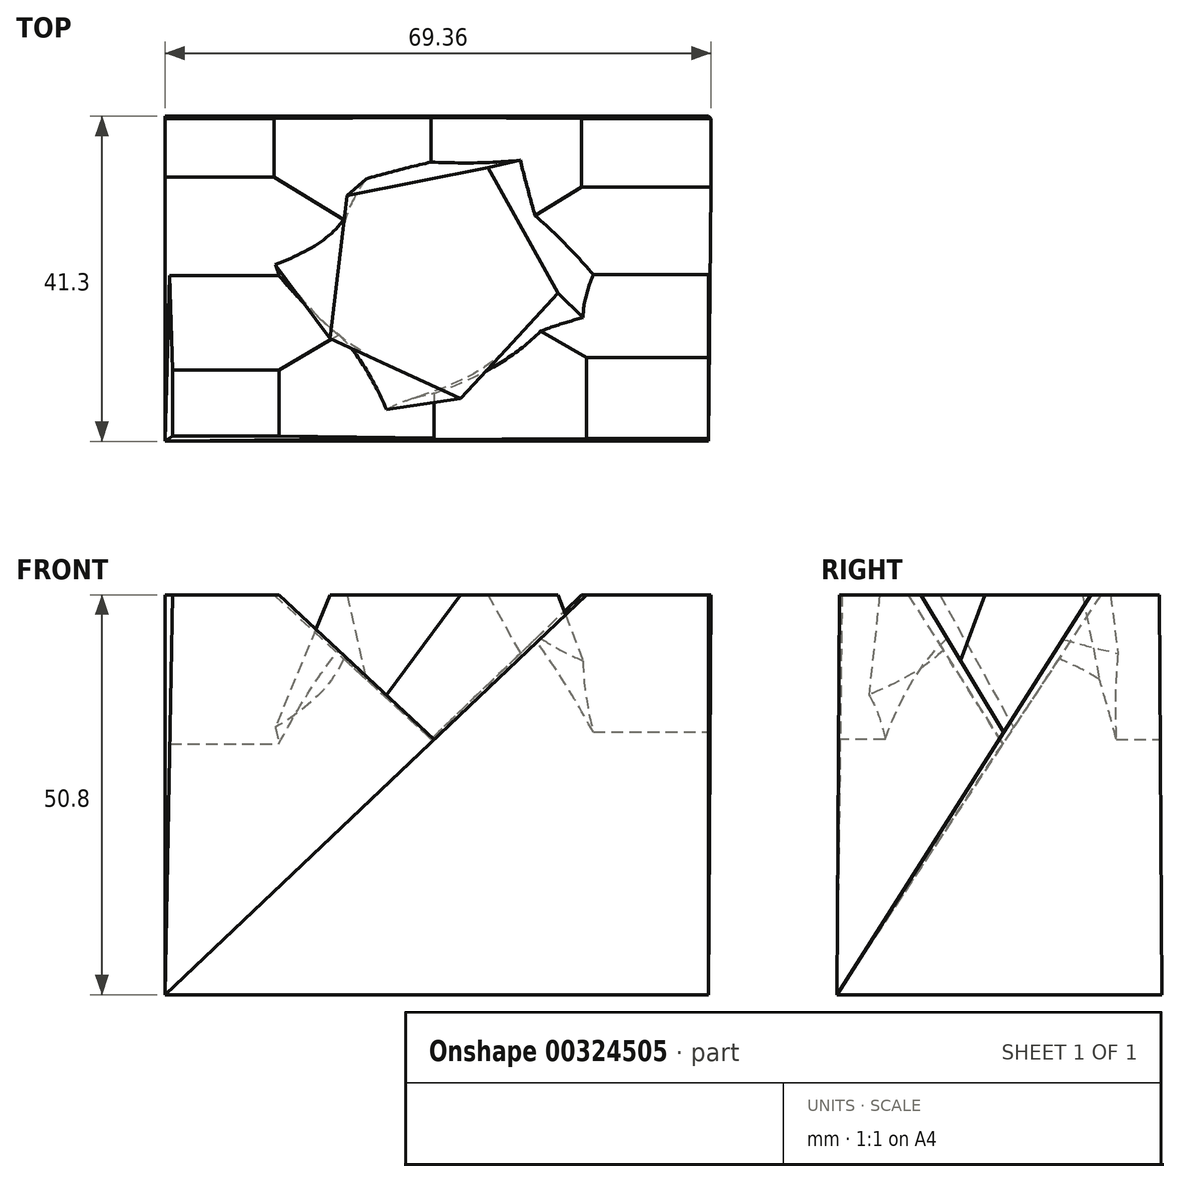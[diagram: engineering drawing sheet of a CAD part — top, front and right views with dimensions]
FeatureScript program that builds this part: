
annotation { "Feature Type Name" : "Feature", "Feature Type Description" : "" }
export const myFeature = defineFeature(function(context is Context, id is Id, definition is map)
    precondition{}
    {
        {
            var Q0;
            Q0=qCreatedBy(makeId("Top.planeOp"),FACE);
            var sketch = newSketch(context, id + "F0", { "sketchPlane" : qUnion([Q0])});
            skLineSegment(sketch, "E0.bottom", {"start": v(34.52, 20.65) * mm, "end": v(-34.52, 20.65) * mm});
            skLineSegment(sketch, "E0.top", {"start": v(34.52, -20.65) * mm, "end": v(-34.52, -20.65) * mm});
            skLineSegment(sketch, "E0.left", {"start": v(34.52, 20.65) * mm, "end": v(34.52, -20.65) * mm});
            skLineSegment(sketch, "E0.right", {"start": v(-34.52, 20.65) * mm, "end": v(-34.52, -20.65) * mm});
            skPoint(sketch, "E0.middle", {"position": v(0, 0) * mm});
            skSolve(sketch);
        }
        {
            var Q0;
            Q0=qCreatedBy(makeId("Top.planeOp"),FACE);
            cPlane(context, id + "F1", {"entities" : qUnion([Q0]), "cplaneType" : CPlaneType.OFFSET, "offset" : 50.8 * mm, "width" : 152.4 * mm, "height" : 152.4 * mm});
        }
        {
            var Q0;
            Q0=qCreatedBy(id+"F1.planeOp",FACE);
            var sketch = newSketch(context, id + "F2", { "sketchPlane" : qUnion([Q0])});
            skLineSegment(sketch, "E1.bottom", {"start": v(-34.52, 20.33) * mm, "end": v(-20.65, 20.33) * mm});
            skLineSegment(sketch, "E1.top", {"start": v(-34.52, 12.9) * mm, "end": v(-20.65, 12.9) * mm});
            skLineSegment(sketch, "E1.left", {"start": v(-34.52, 20.33) * mm, "end": v(-34.52, 12.9) * mm});
            skLineSegment(sketch, "E1.right", {"start": v(-20.65, 20.33) * mm, "end": v(-20.65, 12.9) * mm});
            skLineSegment(sketch, "E2.bottom", {"start": v(34.84, 20.33) * mm, "end": v(18.39, 20.33) * mm});
            skLineSegment(sketch, "E2.top", {"start": v(34.84, 11.61) * mm, "end": v(18.39, 11.61) * mm});
            skLineSegment(sketch, "E2.left", {"start": v(34.84, 20.33) * mm, "end": v(34.84, 11.61) * mm});
            skLineSegment(sketch, "E2.right", {"start": v(18.39, 20.33) * mm, "end": v(18.39, 11.61) * mm});
            skLineSegment(sketch, "E3.bottom", {"start": v(-33.55, -20) * mm, "end": v(-20, -20) * mm});
            skLineSegment(sketch, "E3.top", {"start": v(-33.55, -11.61) * mm, "end": v(-20, -11.61) * mm});
            skLineSegment(sketch, "E3.left", {"start": v(-33.55, -20) * mm, "end": v(-33.55, -11.61) * mm});
            skLineSegment(sketch, "E3.right", {"start": v(-20, -20) * mm, "end": v(-20, -11.61) * mm});
            skLineSegment(sketch, "E4.bottom", {"start": v(34.52, -20.33) * mm, "end": v(19.03, -20.33) * mm});
            skLineSegment(sketch, "E4.top", {"start": v(34.52, -10) * mm, "end": v(19.03, -10) * mm});
            skLineSegment(sketch, "E4.left", {"start": v(34.52, -20.33) * mm, "end": v(34.52, -10) * mm});
            skLineSegment(sketch, "E4.right", {"start": v(19.03, -20.33) * mm, "end": v(19.03, -10) * mm});
            skCircle(sketch, "E5.cCircle", {"center": v(0, 0) * mm, "radius": 12.57 * mm, "construction": true});
            skLineSegment(sketch, "E5.0", {"start": v(6.52, 14.1) * mm, "end": v(15.42, -1.84) * mm});
            skLineSegment(sketch, "E5.1", {"start": v(15.42, -1.84) * mm, "end": v(3.02, -15.24) * mm});
            skLineSegment(sketch, "E5.2", {"start": v(3.02, -15.24) * mm, "end": v(-13.56, -7.58) * mm});
            skLineSegment(sketch, "E5.3", {"start": v(-13.56, -7.58) * mm, "end": v(-11.4, 10.55) * mm});
            skLineSegment(sketch, "E5.4", {"start": v(-11.4, 10.55) * mm, "end": v(6.52, 14.1) * mm});
            skPoint(sketch, "E5.0.midPoint", {"position": v(10.97, 6.13) * mm});
            skSolve(sketch);
        }
        {
            var Q0;
            Q0=makeQuery(id+"F0.imprint","IMPRINT",FACE,{"disambiguationData":[TD([[makeQuery(id+"F0.imprint","IMPRINT",EDGE,{"derivedFrom":sQuery(id+"F0.wireOp",EDGE,"E0.bottom")}),1.0]])]});
            var Q1;
            Q1=makeQuery(id+"F2.imprint","IMPRINT",FACE,{"disambiguationData":[TD([[makeQuery(id+"F2.imprint","IMPRINT",EDGE,{"derivedFrom":sQuery(id+"F2.wireOp",EDGE,"E2.bottom")}),1.0]])]});
            loft(context, id + "F3", {"sheetProfilesArray" : [{ "sheetProfileEntities" : qUnion([Q0]) }, { "sheetProfileEntities" : qUnion([Q1]) }]});
        }
        {
            var Q1;
            Q1=makeQuery(id+"F3.opLoft","CAP_FACE",FACE,{"disambiguationData":[OSD([makeQuery(id+"F0.imprint","IMPRINT",FACE,{"disambiguationData":[TD([[makeQuery(id+"F0.imprint","IMPRINT",EDGE,{"derivedFrom":sQuery(id+"F0.wireOp",EDGE,"E0.bottom")}),1.0]])]})])],"isStart":true});
            var Q2;
            Q2=makeQuery(id+"F2.imprint","IMPRINT",FACE,{"disambiguationData":[TD([[makeQuery(id+"F2.imprint","IMPRINT",EDGE,{"derivedFrom":sQuery(id+"F2.wireOp",EDGE,"E4.bottom")}),-1.0]])]});
            loft(context, id + "F4", {"operationType" : NewBodyOperationType.ADD, "sheetProfilesArray" : [{ "sheetProfileEntities" : qUnion([Q1]) }, { "sheetProfileEntities" : qUnion([Q2]) }]});
        }
        {
            var Q1;
            Q1=makeQuery(id+"F2.imprint","IMPRINT",FACE,{"disambiguationData":[TD([[makeQuery(id+"F2.imprint","IMPRINT",EDGE,{"derivedFrom":sQuery(id+"F2.wireOp",EDGE,"E1.bottom")}),-1.0]])]});
            var Q2;
            Q2=makeQuery(id+"F0.imprint","IMPRINT",FACE,{"disambiguationData":[TD([[makeQuery(id+"F0.imprint","IMPRINT",EDGE,{"derivedFrom":sQuery(id+"F0.wireOp",EDGE,"E0.bottom")}),1.0]])]});
            loft(context, id + "F5", {"operationType" : NewBodyOperationType.ADD, "sheetProfilesArray" : [{ "sheetProfileEntities" : qUnion([Q1]) }, { "sheetProfileEntities" : qUnion([Q2]) }]});
        }
        {
            var Q1;
            Q1=makeQuery(id+"F2.imprint","IMPRINT",FACE,{"disambiguationData":[TD([[makeQuery(id+"F2.imprint","IMPRINT",EDGE,{"derivedFrom":sQuery(id+"F2.wireOp",EDGE,"E3.bottom")}),1.0]])]});
            var Q2;
            Q2=makeQuery(id+"F0.imprint","IMPRINT",FACE,{"disambiguationData":[TD([[makeQuery(id+"F0.imprint","IMPRINT",EDGE,{"derivedFrom":sQuery(id+"F0.wireOp",EDGE,"E0.bottom")}),1.0]])]});
            loft(context, id + "F6", {"operationType" : NewBodyOperationType.ADD, "sheetProfilesArray" : [{ "sheetProfileEntities" : qUnion([Q1]) }, { "sheetProfileEntities" : qUnion([Q2]) }]});
        }
        {
            var Q1;
            Q1=makeQuery(id+"F2.imprint","IMPRINT",FACE,{"disambiguationData":[TD([[makeQuery(id+"F2.imprint","IMPRINT",EDGE,{"derivedFrom":sQuery(id+"F2.wireOp",EDGE,"E5.0")}),-1.0]])]});
            var Q2;
            Q2=makeQuery(id+"F0.imprint","IMPRINT",FACE,{"disambiguationData":[TD([[makeQuery(id+"F0.imprint","IMPRINT",EDGE,{"derivedFrom":sQuery(id+"F0.wireOp",EDGE,"E0.bottom")}),1.0]])]});
            loft(context, id + "F7", {"operationType" : NewBodyOperationType.ADD, "sheetProfilesArray" : [{ "sheetProfileEntities" : qUnion([Q1]) }, { "sheetProfileEntities" : qUnion([Q2]) }]});
        }
    });
